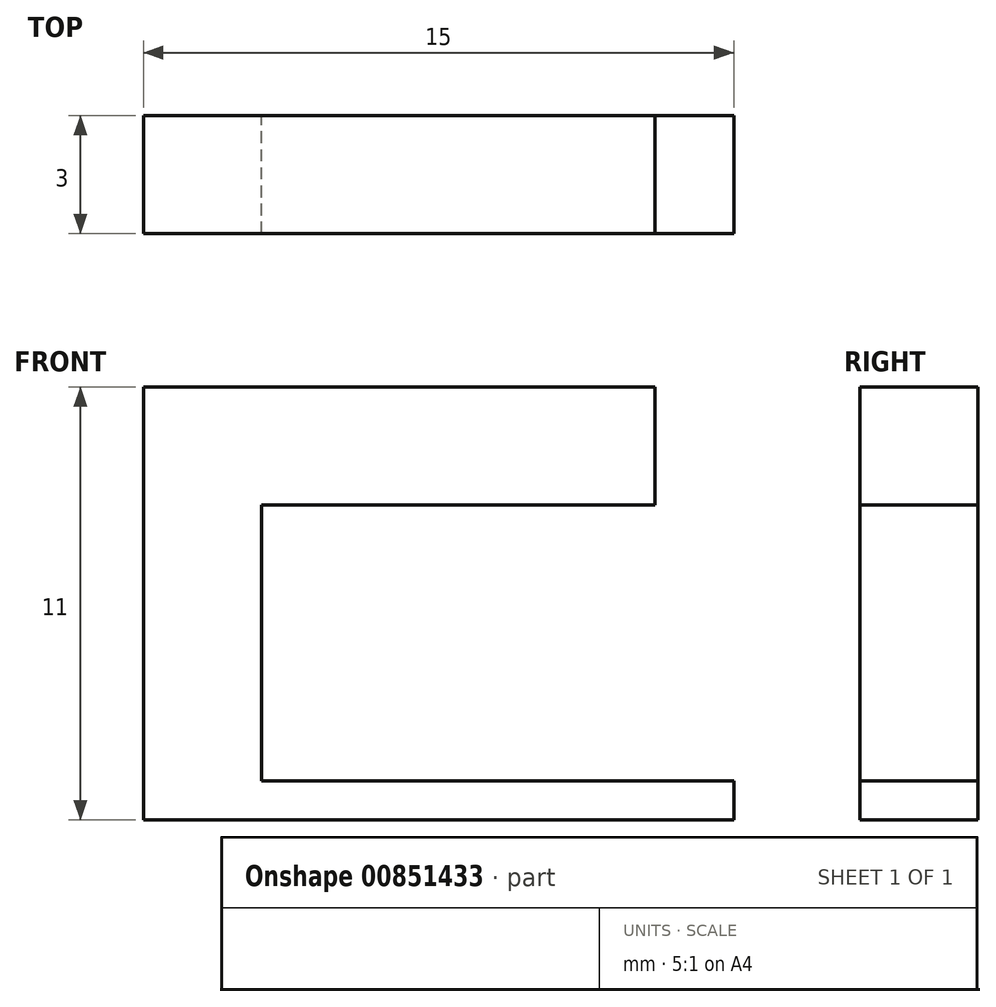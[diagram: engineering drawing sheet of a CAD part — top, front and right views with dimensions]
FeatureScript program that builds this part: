
annotation { "Feature Type Name" : "Feature", "Feature Type Description" : "" }
export const myFeature = defineFeature(function(context is Context, id is Id, definition is map)
    precondition{}
    {
        {
            var Q0;
            Q0=qCreatedBy(makeId("Top.planeOp"),FACE);
            var sketch = newSketch(context, id + "F0", { "sketchPlane" : qUnion([Q0])});
            skLineSegment(sketch, "E0.bottom", {"start": v(7.5, -1.5) * mm, "end": v(-7.5, -1.5) * mm});
            skLineSegment(sketch, "E0.top", {"start": v(7.5, 1.5) * mm, "end": v(-7.5, 1.5) * mm});
            skLineSegment(sketch, "E0.left", {"start": v(7.5, -1.5) * mm, "end": v(7.5, 1.5) * mm});
            skLineSegment(sketch, "E0.right", {"start": v(-7.5, -1.5) * mm, "end": v(-7.5, 1.5) * mm});
            skPoint(sketch, "E0.middle", {"position": v(0, 0) * mm});
            skSolve(sketch);
        }
        {
            var Q0;
            Q0 = qSketchRegion(id + "F0", true);
            extrude(context, id + "F1", {"entities" : qUnion([Q0]), "depth" : 1 * mm, "offsetDistance" : 25 * mm});
        }
        {
            var Q0;
            Q0=makeQuery(id+"F1.opExtrude","CAP_FACE",FACE,{"disambiguationData":[OSD([sQuery(id+"F0.wireOp",EDGE,"E0.bottom"),sQuery(id+"F0.wireOp",EDGE,"E0.top"),sQuery(id+"F0.wireOp",EDGE,"E0.left"),sQuery(id+"F0.wireOp",EDGE,"E0.right")])],"isStart":false});
            var sketch = newSketch(context, id + "F2", { "sketchPlane" : qUnion([Q0])});
            skLineSegment(sketch, "E1.bottom", {"start": v(-4.5, -1.5) * mm, "end": v(-7.5, -1.5) * mm});
            skLineSegment(sketch, "E1.top", {"start": v(-4.5, 1.5) * mm, "end": v(-7.5, 1.5) * mm});
            skLineSegment(sketch, "E1.left", {"start": v(-4.5, -1.5) * mm, "end": v(-4.5, 1.5) * mm});
            skLineSegment(sketch, "E1.right", {"start": v(-7.5, -1.5) * mm, "end": v(-7.5, 1.5) * mm});
            skPoint(sketch, "E1.middle", {"position": v(-6, 0) * mm});
            skPoint(sketch, "E2", {"position": v(-7.5, 0) * mm});
            skSolve(sketch);
        }
        {
            var Q0;
            Q0 = qSketchRegion(id + "F2", true);
            extrude(context, id + "F3", {"entities" : qUnion([Q0]), "operationType" : NewBodyOperationType.ADD, "depth" : 10 * mm, "offsetDistance" : 25 * mm});
        }
        {
            var Q0;
            Q0=makeQuery(id+"F3.opExtrude","SWEPT_FACE",FACE,{"disambiguationData":[OSD([sQuery(id+"F2.wireOp",EDGE,"E1.left")])]});
            var sketch = newSketch(context, id + "F4", { "sketchPlane" : qUnion([Q0])});
            skLineSegment(sketch, "E3.bottom", {"start": v(-1.5, 11) * mm, "end": v(1.5, 11) * mm});
            skLineSegment(sketch, "E3.top", {"start": v(-1.5, 8) * mm, "end": v(1.5, 8) * mm});
            skLineSegment(sketch, "E3.left", {"start": v(-1.5, 11) * mm, "end": v(-1.5, 8) * mm});
            skLineSegment(sketch, "E3.right", {"start": v(1.5, 11) * mm, "end": v(1.5, 8) * mm});
            skSolve(sketch);
        }
        {
            var Q0;
            Q0 = qSketchRegion(id + "F4", true);
            extrude(context, id + "F5", {"entities" : qUnion([Q0]), "operationType" : NewBodyOperationType.ADD, "depth" : 10 * mm, "offsetDistance" : 25 * mm});
        }
    });
